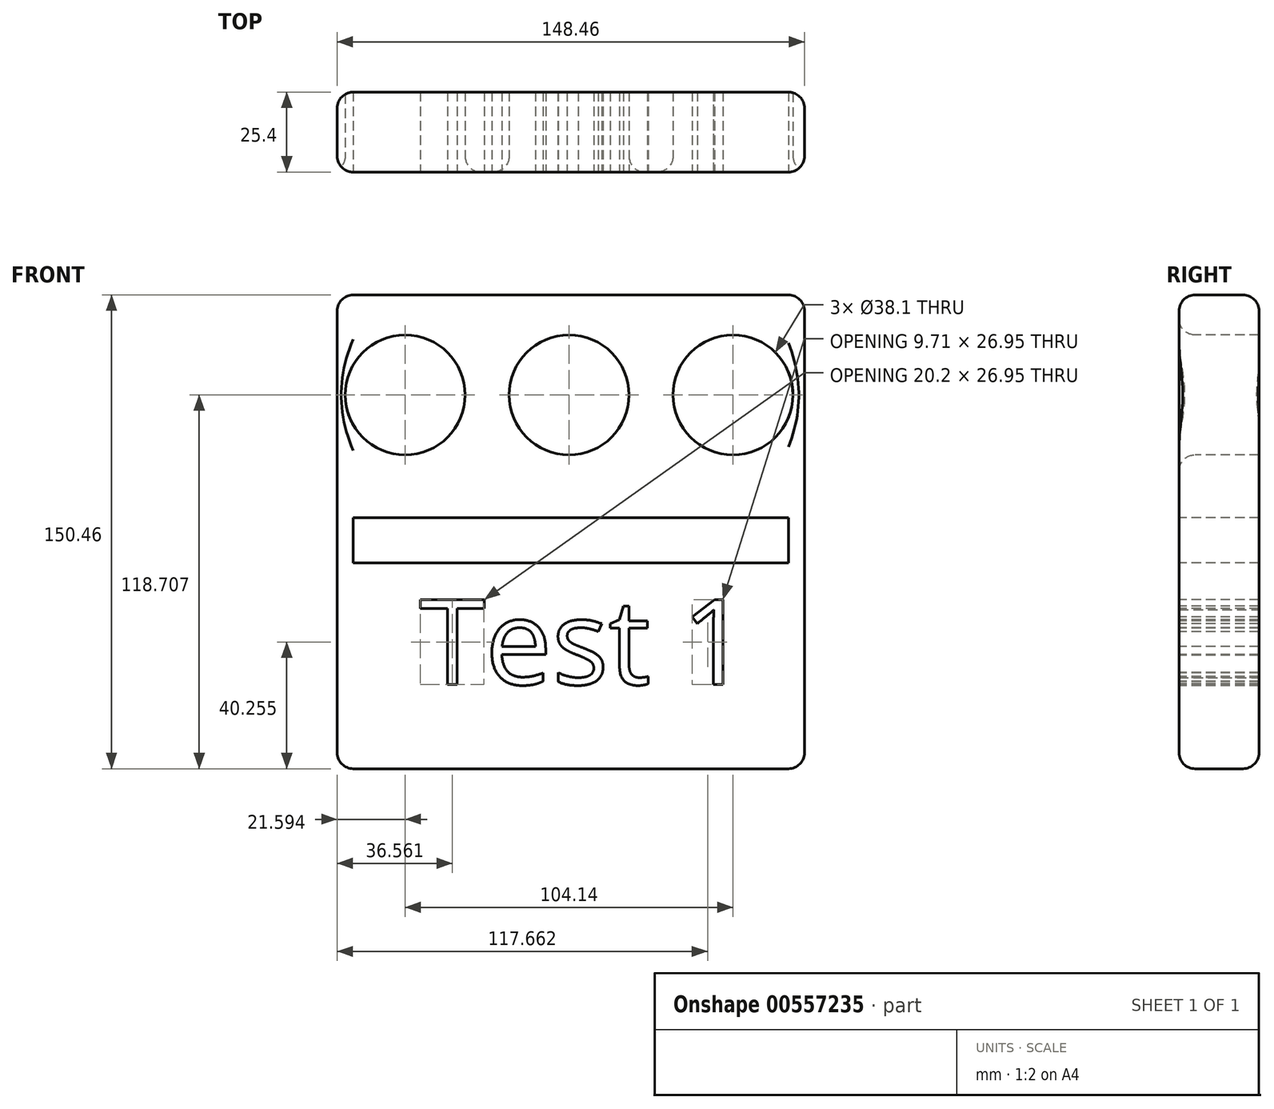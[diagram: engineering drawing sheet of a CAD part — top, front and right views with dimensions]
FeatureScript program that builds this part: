
annotation { "Feature Type Name" : "Feature", "Feature Type Description" : "" }
export const myFeature = defineFeature(function(context is Context, id is Id, definition is map)
    precondition{}
    {
        {
            var Q0;
            Q0=qCreatedBy(makeId("Front.planeOp"),FACE);
            var sketch = newSketch(context, id + "F0", { "sketchPlane" : qUnion([Q0])});
            skLineSegment(sketch, "E0.bottom", {"start": v(-74.23, 77.9) * mm, "end": v(74.23, 77.9) * mm});
            skLineSegment(sketch, "E0.top", {"start": v(-74.23, -72.56) * mm, "end": v(74.23, -72.56) * mm});
            skLineSegment(sketch, "E0.left", {"start": v(-74.23, 77.9) * mm, "end": v(-74.23, -72.56) * mm});
            skLineSegment(sketch, "E0.right", {"start": v(74.23, 77.9) * mm, "end": v(74.23, -72.56) * mm});
            skSolve(sketch);
        }
        {
            var Q0;
            Q0=makeQuery(id+"F0.imprint","IMPRINT",FACE,{"disambiguationData":[TD([[makeQuery(id+"F0.imprint","IMPRINT",EDGE,{"derivedFrom":sQuery(id+"F0.wireOp",EDGE,"E0.bottom")}),-1.0]])]});
            extrude(context, id + "F1", {"entities" : qUnion([Q0]), "depth" : 25.4 * mm, "offsetDistance" : 25.4 * mm});
        }
        {
            var Q0;
            Q0=makeQuery(id+"F1.opExtrude","CAP_FACE",FACE,{"disambiguationData":[OSD([sQuery(id+"F0.wireOp",EDGE,"E0.bottom"),sQuery(id+"F0.wireOp",EDGE,"E0.top"),sQuery(id+"F0.wireOp",EDGE,"E0.left"),sQuery(id+"F0.wireOp",EDGE,"E0.right")])],"isStart":false});
            var sketch = newSketch(context, id + "F2", { "sketchPlane" : qUnion([Q0])});
            skCircle(sketch, "E1", {"center": v(-52.64, 46.15) * mm, "radius": 19.05 * mm});
            skCircle(sketch, "E2.1.0.0", {"center": v(-0.57, 46.15) * mm, "radius": 19.05 * mm});
            skCircle(sketch, "E2.2.0.0", {"center": v(51.5, 46.15) * mm, "radius": 19.05 * mm});
            skLineSegment(sketch, "E2.direction1", {"start": v(-52.64, 46.15) * mm, "end": v(-0.57, 46.15) * mm, "construction": true});
            skSolve(sketch);
        }
        {
            var Q0;
            Q0=makeQuery(id+"F2.imprint","IMPRINT",FACE,{"disambiguationData":[TD([[makeQuery(id+"F2.imprint","IMPRINT",EDGE,{"derivedFrom":sQuery(id+"F2.wireOp",EDGE,"E1")}),1.0]])]});
            var Q1;
            Q1=makeQuery(id+"F2.imprint","IMPRINT",FACE,{"disambiguationData":[TD([[makeQuery(id+"F2.imprint","IMPRINT",EDGE,{"derivedFrom":sQuery(id+"F2.wireOp",EDGE,"E2.1.0.0")}),1.0]])]});
            var Q2;
            Q2=makeQuery(id+"F2.imprint","IMPRINT",FACE,{"disambiguationData":[TD([[makeQuery(id+"F2.imprint","IMPRINT",EDGE,{"derivedFrom":sQuery(id+"F2.wireOp",EDGE,"E2.2.0.0")}),1.0]])]});
            extrude(context, id + "F3", {"entities" : qUnion([Q0, Q1, Q2]), "operationType" : NewBodyOperationType.REMOVE, "endBound" : BoundingType.THROUGH_ALL, "oppositeDirection" : true, "depth" : 25.4 * mm, "offsetDistance" : 25.4 * mm});
        }
        {
            var Q0;
            Q0=makeQuery(id+"F1.opExtrude","SWEPT_EDGE",EDGE,{"disambiguationData":[OSD([sQuery(id+"F0.wireOp",EDGE,"E0.top"),sQuery(id+"F0.wireOp",EDGE,"E0.right")])]});
            var Q1;
            Q1=makeQuery(id+"F1.opExtrude","SWEPT_EDGE",EDGE,{"disambiguationData":[OSD([sQuery(id+"F0.wireOp",EDGE,"E0.bottom"),sQuery(id+"F0.wireOp",EDGE,"E0.left")])]});
            var Q2;
            Q2=makeQuery(id+"F1.opExtrude","CAP_EDGE",EDGE,{"disambiguationData":[OSD([sQuery(id+"F0.wireOp",EDGE,"E0.bottom")])],"isStart":true});
            var Q3;
            Q3=makeQuery(id+"F1.opExtrude","CAP_EDGE",EDGE,{"disambiguationData":[OSD([sQuery(id+"F0.wireOp",EDGE,"E0.left")])],"isStart":true});
            var Q4;
            Q4=makeQuery(id+"F1.opExtrude","CAP_EDGE",EDGE,{"disambiguationData":[OSD([sQuery(id+"F0.wireOp",EDGE,"E0.top")])],"isStart":true});
            var Q5;
            Q5=makeQuery(id+"F1.opExtrude","CAP_EDGE",EDGE,{"disambiguationData":[OSD([sQuery(id+"F0.wireOp",EDGE,"E0.right")])],"isStart":true});
            var Q6;
            Q6=makeQuery(id+"F1.opExtrude","CAP_FACE",FACE,{"disambiguationData":[OSD([sQuery(id+"F0.wireOp",EDGE,"E0.bottom"),sQuery(id+"F0.wireOp",EDGE,"E0.top"),sQuery(id+"F0.wireOp",EDGE,"E0.left"),sQuery(id+"F0.wireOp",EDGE,"E0.right")])],"isStart":false});
            fillet(context, id + "F4", {"entities" : qUnion([Q0, Q1, Q2, Q3, Q4, Q5, Q6]), "radius" : 5.08 * mm, "tangentPropagation" : true, "allowEdgeOverflow" : false});
        }
        {
            var Q0;
            Q0=makeQuery(id+"F4.opFillet","BLEND_EDGE",EDGE,{"blendedFrom":[makeQuery(id+"F1.opExtrude","CAP_EDGE",EDGE,{"disambiguationData":[OSD([sQuery(id+"F0.wireOp",EDGE,"E0.top")])],"isStart":false}),makeQuery(id+"F1.opExtrude","CAP_EDGE",EDGE,{"disambiguationData":[OSD([sQuery(id+"F0.wireOp",EDGE,"E0.left")])],"isStart":false})],"blendedInto":[]});
            var Q1;
            Q1=makeQuery(id+"F4.opFillet","BLEND_EDGE",EDGE,{"blendedFrom":[makeQuery(id+"F1.opExtrude","CAP_EDGE",EDGE,{"disambiguationData":[OSD([sQuery(id+"F0.wireOp",EDGE,"E0.bottom")])],"isStart":false}),makeQuery(id+"F1.opExtrude","CAP_EDGE",EDGE,{"disambiguationData":[OSD([sQuery(id+"F0.wireOp",EDGE,"E0.right")])],"isStart":false})],"blendedInto":[]});
            fillet(context, id + "F5", {"entities" : qUnion([Q0, Q1]), "radius" : 5.08 * mm, "tangentPropagation" : true, "allowEdgeOverflow" : false});
        }
        {
            var Q0;
            Q0=makeQuery(id+"F1.opExtrude","CAP_FACE",FACE,{"disambiguationData":[OSD([sQuery(id+"F0.wireOp",EDGE,"E0.bottom"),sQuery(id+"F0.wireOp",EDGE,"E0.top"),sQuery(id+"F0.wireOp",EDGE,"E0.left"),sQuery(id+"F0.wireOp",EDGE,"E0.right")])],"isStart":false});
            var sketch = newSketch(context, id + "F6", { "sketchPlane" : qUnion([Q0])});
            skLineSegment(sketch, "E3.bottom", {"start": v(69.15, 7.19) * mm, "end": v(-69.15, 7.19) * mm});
            skLineSegment(sketch, "E3.top", {"start": v(69.15, -7.19) * mm, "end": v(-69.15, -7.19) * mm});
            skLineSegment(sketch, "E3.left", {"start": v(69.15, 7.19) * mm, "end": v(69.15, -7.19) * mm});
            skLineSegment(sketch, "E3.right", {"start": v(-69.15, 7.19) * mm, "end": v(-69.15, -7.19) * mm});
            skPoint(sketch, "E3.middle", {"position": v(0, 0) * mm});
            skSolve(sketch);
        }
        {
            var Q0;
            Q0=makeQuery(id+"F6.imprint","IMPRINT",FACE,{"disambiguationData":[TD([[makeQuery(id+"F6.imprint","IMPRINT",EDGE,{"derivedFrom":sQuery(id+"F6.wireOp",EDGE,"E3.bottom")}),1.0]])]});
            extrude(context, id + "F7", {"entities" : qUnion([Q0]), "operationType" : NewBodyOperationType.REMOVE, "endBound" : BoundingType.THROUGH_ALL, "oppositeDirection" : true, "depth" : 25.4 * mm, "offsetDistance" : 25.4 * mm});
        }
        {
            var Q0;
            {var subQ0=sQuery(id+"F0.wireOp",EDGE,"E0.left");var subQ2=sQuery(id+"F0.wireOp",EDGE,"E0.top");var subQ4=sQuery(id+"F0.wireOp",EDGE,"E0.right");Q0=makeQuery(id+"F7.boolean.opBoolean","SPLIT",FACE,{"disambiguationData":[TD([makeQuery(id+"F7.opExtrude","SWEPT_FACE",FACE,{"disambiguationData":[OSD([sQuery(id+"F6.wireOp",EDGE,"E3.top")])]})])],"derivedFrom":makeQuery(id+"F1.opExtrude","CAP_FACE",FACE,{"disambiguationData":[OSD([sQuery(id+"F0.wireOp",EDGE,"E0.bottom"),subQ2,subQ0,subQ4])],"isStart":false})});}
            var sketch = newSketch(context, id + "F8", { "sketchPlane" : qUnion([Q0])});
            skText(sketch, "E4", { "text": "Test 1\n", "fontName": "OpenSans-Regular.ttf"});
            const initialGuessF8  = {"E4": [-0.0481, -0.04578, 1, 0, 0.02718]};
            skSetInitialGuess(sketch, initialGuessF8);
            skSolve(sketch);
        }
        {
            var Q0;
            Q0 = qSketchRegion(id + "F8", true);
            extrude(context, id + "F9", {"entities" : qUnion([Q0]), "operationType" : NewBodyOperationType.REMOVE, "endBound" : BoundingType.THROUGH_ALL, "oppositeDirection" : true, "depth" : 25.4 * mm, "offsetDistance" : 25.4 * mm});
        }
    });
